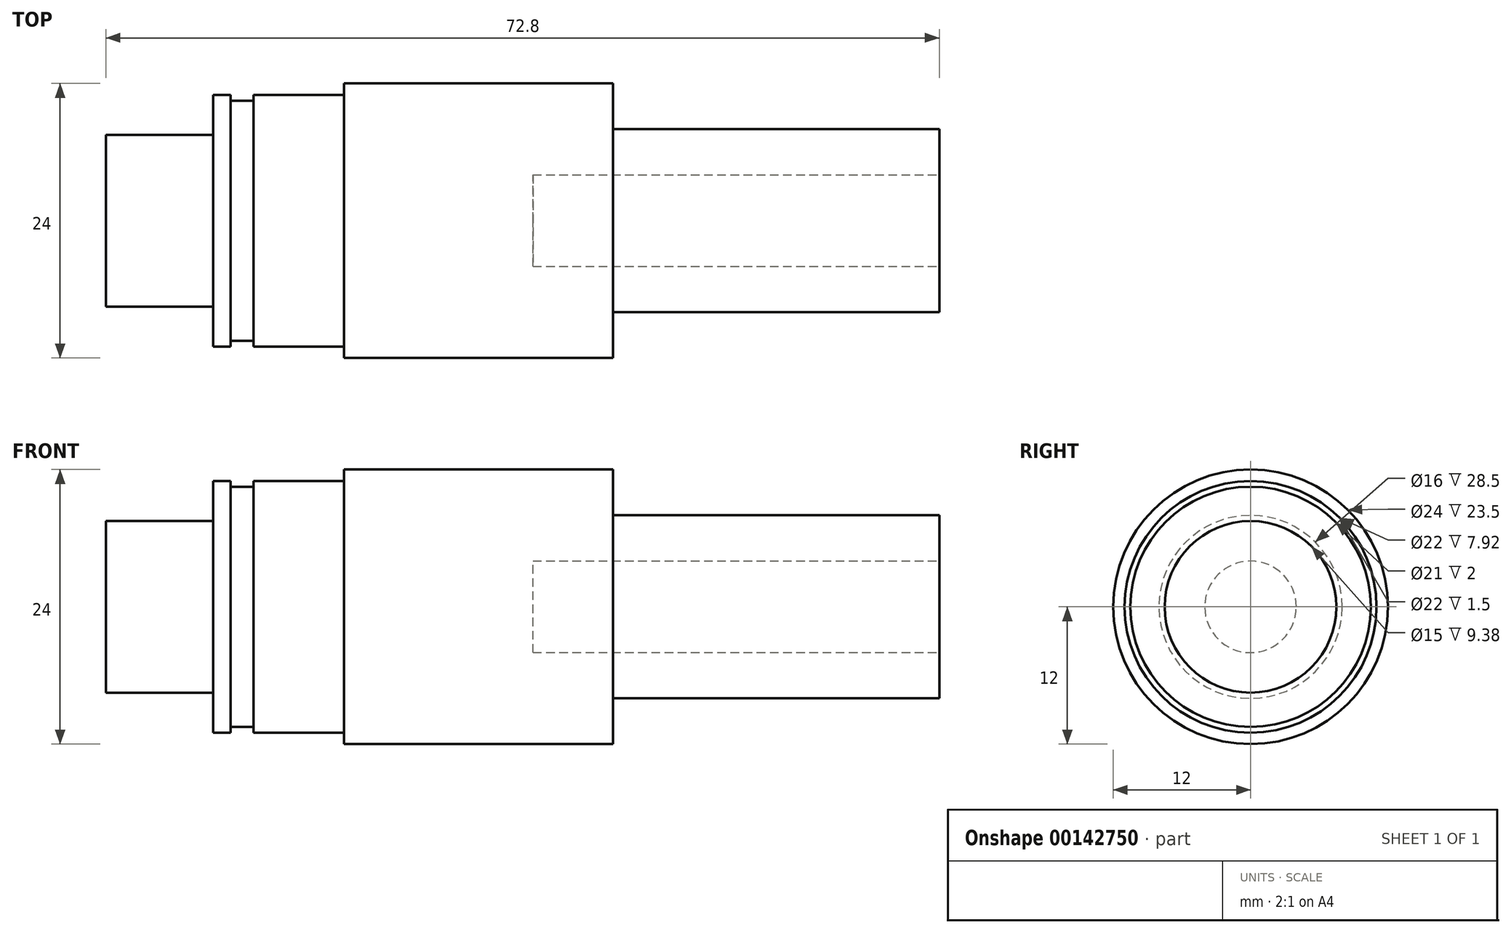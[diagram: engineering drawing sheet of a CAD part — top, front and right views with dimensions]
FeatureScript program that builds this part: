
annotation { "Feature Type Name" : "Feature", "Feature Type Description" : "" }
export const myFeature = defineFeature(function(context is Context, id is Id, definition is map)
    precondition{}
    {
        {
            var Q0;
            Q0=qCreatedBy(makeId("Front.planeOp"),FACE);
            var sketch = newSketch(context, id + "F0", { "sketchPlane" : qUnion([Q0])});
            skLineSegment(sketch, "E0", {"start": v(0, 0) * mm, "end": v(0, 7.5) * mm});
            skLineSegment(sketch, "E1", {"start": v(0, 0) * mm, "end": v(72.8, 0) * mm, "construction": true});
            skLineSegment(sketch, "E2", {"start": v(0, 7.5) * mm, "end": v(9.38, 7.5) * mm});
            skLineSegment(sketch, "E3", {"start": v(9.38, 7.5) * mm, "end": v(9.38, 11) * mm});
            skLineSegment(sketch, "E4", {"start": v(72.8, 8) * mm, "end": v(44.3, 8) * mm});
            skLineSegment(sketch, "E5", {"start": v(44.3, 8) * mm, "end": v(44.3, 12) * mm});
            skLineSegment(sketch, "E6", {"start": v(44.3, 12) * mm, "end": v(20.8, 12) * mm});
            skLineSegment(sketch, "E7", {"start": v(20.8, 12) * mm, "end": v(20.8, 11) * mm});
            skLineSegment(sketch, "E8", {"start": v(20.8, 11) * mm, "end": v(12.88, 11) * mm});
            skLineSegment(sketch, "E9", {"start": v(9.38, 11) * mm, "end": v(10.88, 11) * mm});
            skLineSegment(sketch, "E10", {"start": v(10.88, 11) * mm, "end": v(10.88, 10.5) * mm});
            skLineSegment(sketch, "E11", {"start": v(10.88, 10.5) * mm, "end": v(12.88, 10.5) * mm});
            skLineSegment(sketch, "E12", {"start": v(12.88, 10.5) * mm, "end": v(12.88, 11) * mm});
            skLineSegment(sketch, "E13", {"start": v(72.8, 4) * mm, "end": v(37.3, 4) * mm});
            skLineSegment(sketch, "E14", {"start": v(37.3, 4) * mm, "end": v(37.3, 0) * mm});
            skLineSegment(sketch, "E15", {"start": v(72.8, 4) * mm, "end": v(72.8, 8) * mm});
            skSolve(sketch);
        }
        {
            var Q0;
            Q0=sQuery(id+"F0.wireOp",EDGE,"E0");
            var Q1;
            Q1=sQuery(id+"F0.wireOp",EDGE,"E2");
            var Q2;
            Q2=sQuery(id+"F0.wireOp",EDGE,"E3");
            var Q3;
            Q3=sQuery(id+"F0.wireOp",EDGE,"E2");
            var Q4;
            Q4=sQuery(id+"F0.wireOp",EDGE,"E9");
            var Q5;
            Q5=sQuery(id+"F0.wireOp",EDGE,"E10");
            var Q6;
            Q6=sQuery(id+"F0.wireOp",EDGE,"E11");
            var Q7;
            Q7=sQuery(id+"F0.wireOp",EDGE,"E12");
            var Q8;
            Q8=sQuery(id+"F0.wireOp",EDGE,"E8");
            var Q9;
            Q9=sQuery(id+"F0.wireOp",EDGE,"E7");
            var Q10;
            Q10=sQuery(id+"F0.wireOp",EDGE,"E6");
            var Q11;
            Q11=sQuery(id+"F0.wireOp",EDGE,"E5");
            var Q12;
            Q12=sQuery(id+"F0.wireOp",EDGE,"E4");
            var Q13;
            Q13=sQuery(id+"F0.wireOp",EDGE,"E15");
            var Q14;
            Q14=sQuery(id+"F0.wireOp",EDGE,"E13");
            var Q15;
            Q15=sQuery(id+"F0.wireOp",EDGE,"E14");
            var Q16;
            Q16=sQuery(id+"F0.wireOp",EDGE,"E1");
            revolve(context, id + "F1", {"bodyType" : ToolBodyType.SURFACE, "surfaceEntities" : qUnion([Q0, Q1, Q2, Q3, Q4, Q5, Q6, Q7, Q8, Q9, Q10, Q11, Q12, Q13, Q14, Q15]), "axis" : qUnion([Q16]), "revolveType" : RevolveType.FULL});
        }
    });
